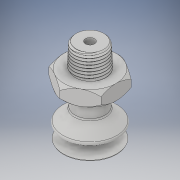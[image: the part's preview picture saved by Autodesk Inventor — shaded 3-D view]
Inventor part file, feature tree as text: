
AUTODESK INVENTOR PART (.ipt)
format: ipt  version: 2019.4 (Build 234330000, 330)  size: 746,496 bytes
history: native  units: mm
features: revolve x1, boolean_combine x1
ambient origin geometry x8: Origin, YZ Plane, XZ Plane, XY Plane, X Axis, Y Axis, Z Axis, Center Point
bodies: Solid1 (feature_tree), Solid2 (feature_tree)
feature tree (2):
  revolve  "Revolve1"  [1 undecoded]
  boolean_combine  "Combine1"
note: 1 required parameter value undecoded (feature->parameter linkage not recoverable at this tier; creation-order binding heuristic only, values carry confidence <= 0.55)
